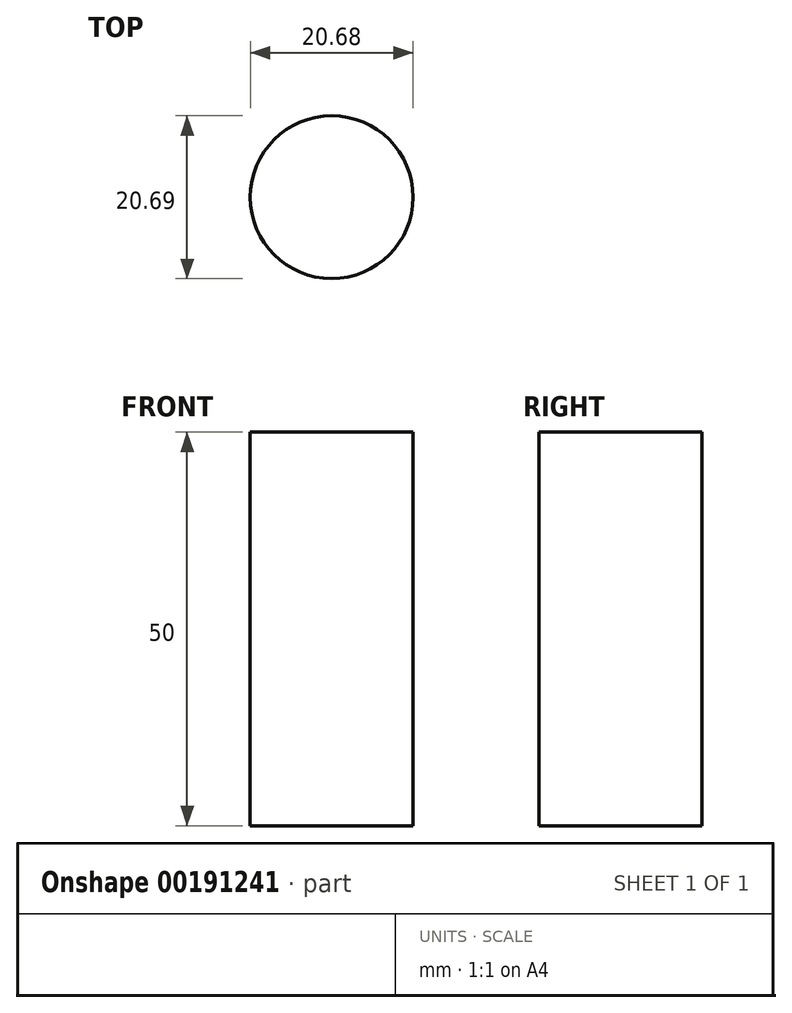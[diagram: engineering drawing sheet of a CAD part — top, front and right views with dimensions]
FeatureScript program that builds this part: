
annotation { "Feature Type Name" : "Feature", "Feature Type Description" : "" }
export const myFeature = defineFeature(function(context is Context, id is Id, definition is map)
    precondition{}
    {
        {
            var Q0;
            Q0=qCreatedBy(makeId("Top.planeOp"),FACE);
            var sketch = newSketch(context, id + "F0", { "sketchPlane" : qUnion([Q0])});
            skLineSegment(sketch, "E0.bottom", {"start": v(0, 0) * mm, "end": v(66.2, 0) * mm});
            skLineSegment(sketch, "E0.top", {"start": v(0.33, 20.13) * mm, "end": v(20.43, 20.13) * mm});
            skLineSegment(sketch, "E0.right", {"start": v(66.2, 0) * mm, "end": v(20.43, 20.13) * mm});
            skLineSegment(sketch, "E1", {"start": v(0, 0) * mm, "end": v(0.33, 20.13) * mm});
            skLineSegment(sketch, "E2", {"start": v(20.43, 20.13) * mm, "end": v(20.43, 0) * mm});
            skLineSegment(sketch, "E3", {"start": v(20.43, 10.06) * mm, "end": v(43.32, 10.06) * mm});
            skArc(sketch, "E4", {"start": v(31.88, 10.06) * mm, "mid": v(20.66, 9.64) * mm, "end": v(16.65, 20.13) * mm});
            skCircle(sketch, "E5", {"center": v(-62.88, 13.49) * mm, "radius": 10.34 * mm});
            skCircle(sketch, "E6", {"center": v(-62.88, 13.49) * mm, "radius": 9.05 * mm});
            skSolve(sketch);
        }
        {
            var Q0;
            Q0=sQuery(id+"F0.wireOp",EDGE,"E5");
            extrude(context, id + "F1", {"bodyType" : ToolBodyType.SURFACE, "surfaceEntities" : qUnion([Q0]), "depth" : 50 * mm});
        }
    });
